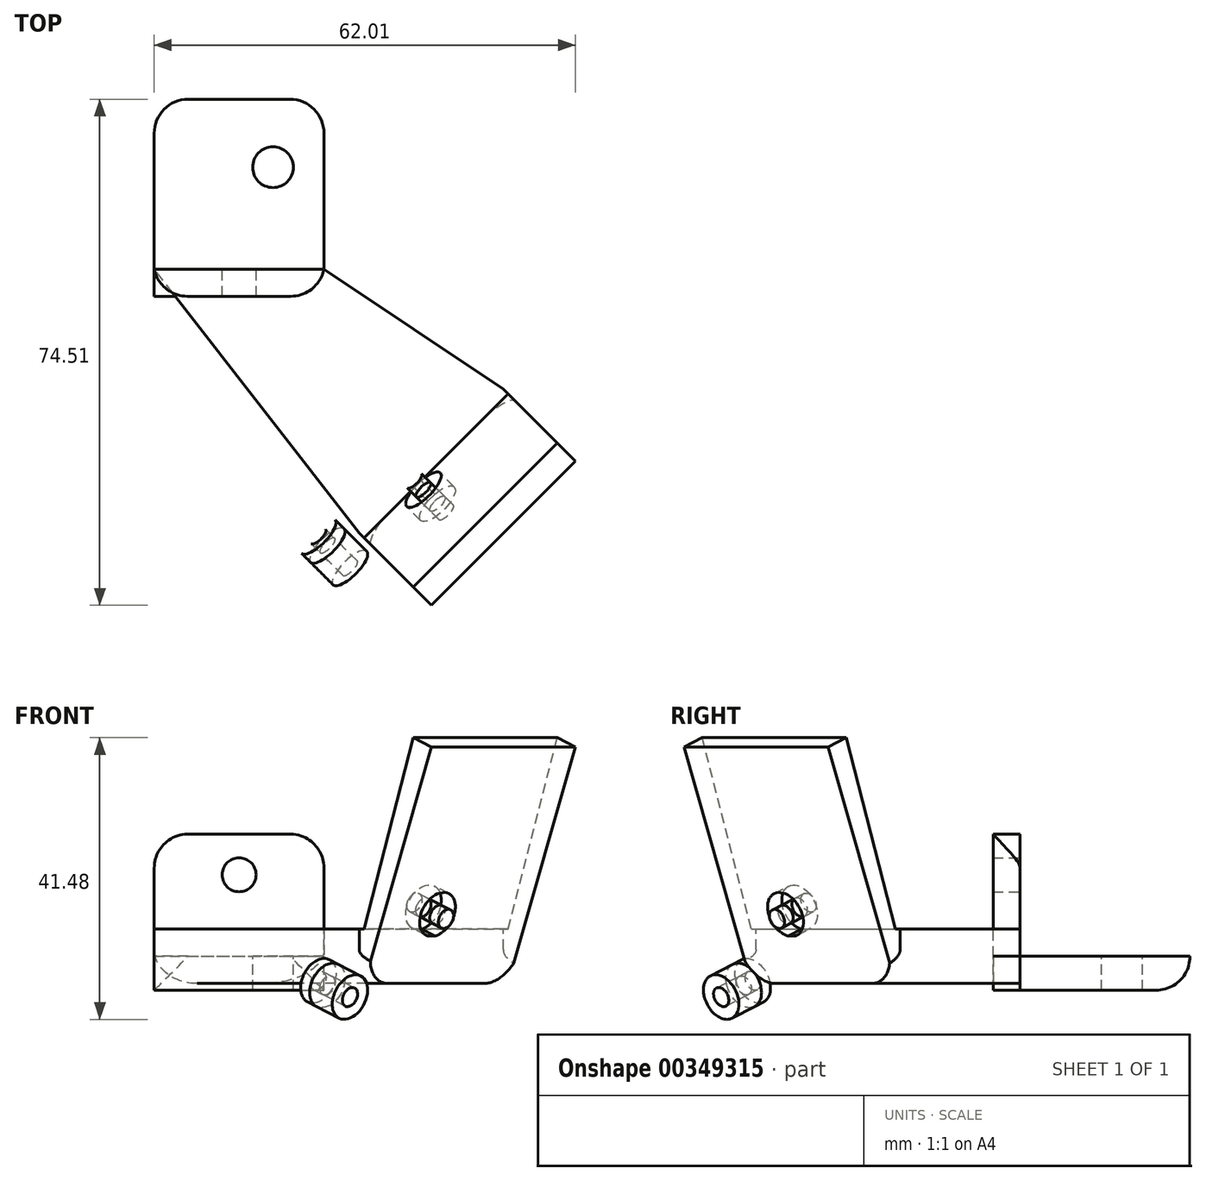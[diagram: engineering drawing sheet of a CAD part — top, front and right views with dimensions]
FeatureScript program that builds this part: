
annotation { "Feature Type Name" : "Feature", "Feature Type Description" : "" }
export const myFeature = defineFeature(function(context is Context, id is Id, definition is map)
    precondition{}
    {
        {
            var Q0;
            Q0=qCreatedBy(makeId("Top.planeOp"),FACE);
            var sketch = newSketch(context, id + "F0", { "sketchPlane" : qUnion([Q0])});
            skLineSegment(sketch, "E0.bottom", {"start": v(-12.5, 0) * mm, "end": v(12.5, 0) * mm});
            skLineSegment(sketch, "E0.top", {"start": v(-12.5, 25) * mm, "end": v(12.5, 25) * mm});
            skLineSegment(sketch, "E0.left", {"start": v(-12.5, 0) * mm, "end": v(-12.5, 25) * mm});
            skLineSegment(sketch, "E0.right", {"start": v(12.5, 0) * mm, "end": v(12.5, 25) * mm});
            skCircle(sketch, "E1", {"center": v(5, 15) * mm, "radius": 3 * mm});
            skLineSegment(sketch, "E2.top", {"start": v(-12.5, -4) * mm, "end": v(12.5, -4) * mm});
            skLineSegment(sketch, "E2.left", {"start": v(-12.5, 0) * mm, "end": v(-12.5, -4) * mm});
            skLineSegment(sketch, "E2.right", {"start": v(12.5, 0) * mm, "end": v(12.5, -4) * mm});
            skSolve(sketch);
        }
        {
            var Q0;
            Q0=makeQuery(id+"F0.imprint","IMPRINT",FACE,{"disambiguationData":[TD([[makeQuery(id+"F0.imprint","IMPRINT",EDGE,{"derivedFrom":sQuery(id+"F0.wireOp",EDGE,"E0.top")}),-1.0]])]});
            extrude(context, id + "F1", {"entities" : qUnion([Q0]), "oppositeDirection" : true, "depth" : 5 * mm});
        }
        {
            var Q0;
            Q0=makeQuery(id+"F0.imprint","IMPRINT",FACE,{"disambiguationData":[TD([[makeQuery(id+"F0.imprint","IMPRINT",EDGE,{"derivedFrom":sQuery(id+"F0.wireOp",EDGE,"E0.bottom")}),-1.0]])]});
            extrude(context, id + "F2", {"entities" : qUnion([Q0]), "depth" : 18 * mm});
        }
        {
            var Q0;
            Q0=makeQuery(id+"F2.opExtrude","CAP_FACE",FACE,{"disambiguationData":[OSD([sQuery(id+"F0.wireOp",EDGE,"E0.bottom"),sQuery(id+"F0.wireOp",EDGE,"E2.top"),sQuery(id+"F0.wireOp",EDGE,"E2.left"),sQuery(id+"F0.wireOp",EDGE,"E2.right")])],"isStart":true});
            extrude(context, id + "F3", {"entities" : qUnion([Q0]), "depth" : 5 * mm});
        }
        {
            var Q0;
            Q0=makeQuery(id+"F2.opExtrude","SWEPT_FACE",FACE,{"disambiguationData":[OSD([sQuery(id+"F0.wireOp",EDGE,"E0.bottom")])]});
            var sketch = newSketch(context, id + "F4", { "sketchPlane" : qUnion([Q0])});
            skCircle(sketch, "E3", {"center": v(0, 12) * mm, "radius": 2.5 * mm});
            skSolve(sketch);
        }
        {
            var Q0;
            Q0=makeQuery(id+"F4.imprint","IMPRINT",FACE,{"disambiguationData":[TD([[makeQuery(id+"F4.imprint","IMPRINT",EDGE,{"derivedFrom":sQuery(id+"F4.wireOp",EDGE,"E3")}),1.0]])]});
            extrude(context, id + "F5", {"entities" : qUnion([Q0]), "operationType" : NewBodyOperationType.REMOVE, "oppositeDirection" : true, "depth" : 4 * mm});
        }
        {
            var Q0;
            Q0=qCreatedBy(makeId("Top.planeOp"),FACE);
            var sketch = newSketch(context, id + "F6", { "sketchPlane" : qUnion([Q0])});
            skLineSegment(sketch, "E4", {"start": v(0, 0) * mm, "end": v(28.28, -28.28) * mm});
            skLineSegment(sketch, "E5", {"start": v(0, 0) * mm, "end": v(-12.5, 0) * mm});
            skLineSegment(sketch, "E6", {"start": v(17.68, -38.9) * mm, "end": v(28.28, -28.28) * mm});
            skLineSegment(sketch, "E7.MirrorCS", {"start": v(38.9, -17.68) * mm, "end": v(28.28, -28.28) * mm});
            skLineSegment(sketch, "E8", {"start": v(0, 0) * mm, "end": v(12.5, 0) * mm});
            skLineSegment(sketch, "E9", {"start": v(17.68, -38.9) * mm, "end": v(-12.5, 0) * mm});
            skLineSegment(sketch, "E10", {"start": v(38.9, -17.68) * mm, "end": v(12.5, 0) * mm});
            skSolve(sketch);
        }
        {
            var Q0;
            Q0=makeQuery(id+"F6.imprint","IMPRINT",FACE,{"disambiguationData":[TD([[makeQuery(id+"F6.imprint","IMPRINT",EDGE,{"derivedFrom":sQuery(id+"F6.wireOp",EDGE,"E4")}),-1.0]])]});
            var Q1;
            Q1=makeQuery(id+"F6.imprint","IMPRINT",FACE,{"disambiguationData":[TD([[makeQuery(id+"F6.imprint","IMPRINT",EDGE,{"derivedFrom":sQuery(id+"F6.wireOp",EDGE,"E4")}),1.0]])]});
            extrude(context, id + "F7", {"entities" : qUnion([Q0, Q1]), "endBound" : BoundingType.SYMMETRIC, "oppositeDirection" : true, "depth" : 8 * mm});
        }
        {
            var Q0;
            Q0=makeQuery(id+"F7.opExtrude","SWEPT_FACE",FACE,{"disambiguationData":[OSD([sQuery(id+"F6.wireOp",EDGE,"E6"),sQuery(id+"F6.wireOp",EDGE,"E7.MirrorCS")])]});
            var sketch = newSketch(context, id + "F8", { "sketchPlane" : qUnion([Q0])});
            skLineSegment(sketch, "E11.bottom", {"start": v(15, -4) * mm, "end": v(-15, -4) * mm});
            skLineSegment(sketch, "E11.top", {"start": v(15, 4) * mm, "end": v(-15, 4) * mm});
            skLineSegment(sketch, "E11.left", {"start": v(15, -4) * mm, "end": v(15, 4) * mm});
            skLineSegment(sketch, "E11.right", {"start": v(-15, -4) * mm, "end": v(-15, 4) * mm});
            skSolve(sketch);
        }
        {
            var Q0;
            Q0=makeQuery(id+"F8.imprint","IMPRINT",FACE,{"disambiguationData":[TD([[makeQuery(id+"F8.imprint","IMPRINT",EDGE,{"derivedFrom":sQuery(id+"F8.wireOp",EDGE,"E11.bottom")}),1.0]])]});
            extrude(context, id + "F9", {"entities" : qUnion([Q0]), "operationType" : NewBodyOperationType.ADD, "depth" : 1 * mm});
        }
        {
            var Q0;
            Q0=makeQuery(id+"F9.opExtrude","SWEPT_FACE",FACE,{"disambiguationData":[OSD([sQuery(id+"F8.wireOp",EDGE,"E11.left")])]});
            var sketch = newSketch(context, id + "F10", { "sketchPlane" : qUnion([Q0])});
            skLineSegment(sketch, "E12", {"start": v(-41, 4) * mm, "end": v(-51.26, 32.2) * mm});
            skLineSegment(sketch, "E13", {"start": v(-51.26, 32.2) * mm, "end": v(-55.02, 30.82) * mm});
            skLineSegment(sketch, "E14", {"start": v(-55.02, 30.82) * mm, "end": v(-41, -4) * mm});
            skSolve(sketch);
        }
        {
            var Q0;
            Q0=makeQuery(id+"F10.imprint","IMPRINT",FACE,{"disambiguationData":[TD([[makeQuery(id+"F10.imprint","IMPRINT",EDGE,{"derivedFrom":sQuery(id+"F10.wireOp",EDGE,"E12")}),1.0]])]});
            var Q1;
            Q1=makeQuery(id+"F9.opExtrude","SWEPT_FACE",FACE,{"disambiguationData":[OSD([sQuery(id+"F8.wireOp",EDGE,"E11.right")])]});
            extrude(context, id + "F11", {"entities" : qUnion([Q0]), "operationType" : NewBodyOperationType.ADD, "endBound" : BoundingType.UP_TO_SURFACE, "oppositeDirection" : true, "endBoundEntityFace" : qUnion([Q1]), "depth" : 25 * mm});
        }
        {
            var Q0;
            Q0=makeQuery(id+"F1.opExtrude","CAP_EDGE",EDGE,{"disambiguationData":[OSD([sQuery(id+"F0.wireOp",EDGE,"E0.top")])],"isStart":false});
            var Q1;
            Q1=makeQuery(id+"F2.opExtrude","SWEPT_EDGE",EDGE,{"disambiguationData":[OSD([sQuery(id+"F0.wireOp",EDGE,"E2.top"),sQuery(id+"F0.wireOp",EDGE,"E2.right")])]});
            var Q2;
            Q2=makeQuery(id+"F7.opExtrude","CAP_EDGE",EDGE,{"disambiguationData":[OSD([sQuery(id+"F6.wireOp",EDGE,"E9")])],"isStart":false});
            var Q3;
            Q3=makeQuery(id+"F7.opExtrude","CAP_EDGE",EDGE,{"disambiguationData":[OSD([sQuery(id+"F6.wireOp",EDGE,"E10")])],"isStart":false});
            var Q4;
            Q4=makeQuery(id+"F3.opExtrude","SWEPT_EDGE",EDGE,{"disambiguationData":[OSD([sQuery(id+"F0.wireOp",EDGE,"E2.top"),sQuery(id+"F0.wireOp",EDGE,"E2.right")])]});
            var Q5;
            Q5=makeQuery(id+"F2.opExtrude","CAP_EDGE",EDGE,{"disambiguationData":[OSD([sQuery(id+"F0.wireOp",EDGE,"E2.left")])],"isStart":false});
            var Q6;
            Q6=makeQuery(id+"F1.opExtrude","SWEPT_EDGE",EDGE,{"disambiguationData":[OSD([sQuery(id+"F0.wireOp",EDGE,"E0.top"),sQuery(id+"F0.wireOp",EDGE,"E0.right")])]});
            var Q7;
            Q7=makeQuery(id+"F1.opExtrude","SWEPT_EDGE",EDGE,{"disambiguationData":[OSD([sQuery(id+"F0.wireOp",EDGE,"E0.top"),sQuery(id+"F0.wireOp",EDGE,"E0.left")])]});
            var Q8;
            Q8=makeQuery(id+"F2.opExtrude","CAP_EDGE",EDGE,{"disambiguationData":[OSD([sQuery(id+"F0.wireOp",EDGE,"E2.right")])],"isStart":false});
            var Q9;
            Q9=makeQuery(id+"F2.opExtrude","SWEPT_EDGE",EDGE,{"disambiguationData":[OSD([sQuery(id+"F0.wireOp",EDGE,"E2.top"),sQuery(id+"F0.wireOp",EDGE,"E2.left")])]});
            fillet(context, id + "F12", {"entities" : qUnion([Q0, Q1, Q2, Q3, Q4, Q5, Q6, Q7, Q8, Q9]), "radius" : 5 * mm, "tangentPropagation" : true, "allowEdgeOverflow" : false});
        }
        {
            var Q0;
            Q0=makeQuery(id+"F11.opExtrude","SWEPT_FACE",FACE,{"disambiguationData":[OSD([sQuery(id+"F10.wireOp",EDGE,"E12")])]});
            var sketch = newSketch(context, id + "F13", { "sketchPlane" : qUnion([Q0])});
            skLineSegment(sketch, "E15", {"start": v(15.46, 45.21) * mm, "end": v(5.75, 16.82) * mm});
            skLineSegment(sketch, "E16", {"start": v(15.46, 45.21) * mm, "end": v(13.84, 40.48) * mm});
            skLineSegment(sketch, "E17", {"start": v(15.46, 45.21) * mm, "end": v(6.18, 18.05) * mm});
            skLineSegment(sketch, "E18", {"start": v(6.18, 18.05) * mm, "end": v(15.64, 14.82) * mm});
            skCircle(sketch, "E19", {"center": v(13.84, 40.48) * mm, "radius": 1.5 * mm});
            skCircle(sketch, "E20", {"center": v(15.64, 14.82) * mm, "radius": 1.5 * mm});
            skCircle(sketch, "E21.MirrorC", {"center": v(-3.29, 21.3) * mm, "radius": 1.5 * mm});
            skCircle(sketch, "E22", {"center": v(-3.29, 21.3) * mm, "radius": 3.5 * mm});
            skCircle(sketch, "E23", {"center": v(15.64, 14.82) * mm, "radius": 3.5 * mm});
            skCircle(sketch, "E24", {"center": v(13.84, 40.48) * mm, "radius": 3.5 * mm});
            skSolve(sketch);
        }
        {
            var Q0;
            {var subQ0=sQuery(id+"F13.wireOp",EDGE,"E20");var subQ1=sQuery(id+"F8.wireOp",EDGE,"E11.top");var subQ2=makeQuery(id+"F11.boolean.opBoolean","MERGE",EDGE,{"derivedFrom":[makeQuery(id+"F9.opExtrude","CAP_EDGE",EDGE,{"disambiguationData":[OSD([subQ1])],"isStart":false}),makeQuery(id+"F11.opExtrude","SWEPT_EDGE",EDGE,{"disambiguationData":[OSD([subQ1,sQuery(id+"F8.wireOp",EDGE,"E11.left"),sQuery(id+"F10.wireOp",EDGE,"E12")])]})]});var subQ3=makeQuery(id+"F13.imprint","INTERSECT",VERTEX,{"disambiguationData":[OD(0.0)],"derivedFrom":[subQ2,subQ0]});Q0=makeQuery(id+"F13.imprint","IMPRINT",FACE,{"disambiguationData":[TD([[makeQuery(id+"F13.imprint","IMPRINT",EDGE,{"disambiguationData":[TD([[subQ3,-1.0]])],"derivedFrom":subQ0}),-1.0]])]});}
            var Q1;
            {var subQ0=sQuery(id+"F13.wireOp",EDGE,"E20");var subQ1=sQuery(id+"F13.wireOp",EDGE,"E18");var subQ2=makeQuery(id+"F13.imprint","INTERSECT",VERTEX,{"derivedFrom":[subQ1,subQ0]});Q1=makeQuery(id+"F13.imprint","IMPRINT",FACE,{"disambiguationData":[TD([[makeQuery(id+"F13.imprint","IMPRINT",EDGE,{"disambiguationData":[TD([[subQ2,1.0]])],"derivedFrom":subQ1}),-1.0]])]});}
            var Q2;
            {var subQ0=sQuery(id+"F13.wireOp",EDGE,"E20");var subQ1=sQuery(id+"F13.wireOp",EDGE,"E18");var subQ2=makeQuery(id+"F13.imprint","INTERSECT",VERTEX,{"derivedFrom":[subQ1,subQ0]});Q2=makeQuery(id+"F13.imprint","IMPRINT",FACE,{"disambiguationData":[TD([[makeQuery(id+"F13.imprint","IMPRINT",EDGE,{"disambiguationData":[TD([[subQ2,1.0]])],"derivedFrom":subQ1}),1.0]])]});}
            var Q3;
            {var subQ0=sQuery(id+"F13.wireOp",EDGE,"E21.MirrorC");var subQ1=sQuery(id+"F8.wireOp",EDGE,"E11.top");var subQ2=makeQuery(id+"F11.boolean.opBoolean","MERGE",EDGE,{"derivedFrom":[makeQuery(id+"F9.opExtrude","CAP_EDGE",EDGE,{"disambiguationData":[OSD([subQ1])],"isStart":false}),makeQuery(id+"F11.opExtrude","SWEPT_EDGE",EDGE,{"disambiguationData":[OSD([subQ1,sQuery(id+"F8.wireOp",EDGE,"E11.left"),sQuery(id+"F10.wireOp",EDGE,"E12")])]})]});var subQ3=makeQuery(id+"F13.imprint","INTERSECT",VERTEX,{"disambiguationData":[OD(0.0)],"derivedFrom":[subQ2,subQ0]});Q3=makeQuery(id+"F13.imprint","IMPRINT",FACE,{"disambiguationData":[TD([[makeQuery(id+"F13.imprint","IMPRINT",EDGE,{"disambiguationData":[TD([[subQ3,1.0]])],"derivedFrom":subQ0}),1.0]])]});}
            var Q4;
            {var subQ0=sQuery(id+"F13.wireOp",EDGE,"E21.MirrorC");var subQ1=sQuery(id+"F8.wireOp",EDGE,"E11.top");var subQ2=makeQuery(id+"F11.boolean.opBoolean","MERGE",EDGE,{"derivedFrom":[makeQuery(id+"F9.opExtrude","CAP_EDGE",EDGE,{"disambiguationData":[OSD([subQ1])],"isStart":false}),makeQuery(id+"F11.opExtrude","SWEPT_EDGE",EDGE,{"disambiguationData":[OSD([subQ1,sQuery(id+"F8.wireOp",EDGE,"E11.left"),sQuery(id+"F10.wireOp",EDGE,"E12")])]})]});var subQ3=makeQuery(id+"F13.imprint","INTERSECT",VERTEX,{"disambiguationData":[OD(0.0)],"derivedFrom":[subQ2,subQ0]});Q4=makeQuery(id+"F13.imprint","IMPRINT",FACE,{"disambiguationData":[TD([[makeQuery(id+"F13.imprint","IMPRINT",EDGE,{"disambiguationData":[TD([[subQ3,-1.0]])],"derivedFrom":subQ0}),1.0]])]});}
            var Q5;
            {var subQ0=sQuery(id+"F13.wireOp",EDGE,"E24");var subQ1=sQuery(id+"F13.wireOp",EDGE,"E17");var subQ2=makeQuery(id+"F13.imprint","INTERSECT",VERTEX,{"disambiguationData":[OD(0.0)],"derivedFrom":[subQ1,subQ0]});Q5=makeQuery(id+"F13.imprint","IMPRINT",FACE,{"disambiguationData":[TD([[makeQuery(id+"F13.imprint","IMPRINT",EDGE,{"disambiguationData":[TD([[subQ2,-1.0]])],"derivedFrom":subQ1}),1.0]])]});}
            var Q6;
            {var subQ0=sQuery(id+"F13.wireOp",EDGE,"E24");var subQ1=sQuery(id+"F13.wireOp",EDGE,"E17");var subQ2=makeQuery(id+"F13.imprint","INTERSECT",VERTEX,{"disambiguationData":[OD(0.0)],"derivedFrom":[subQ1,subQ0]});Q6=makeQuery(id+"F13.imprint","IMPRINT",FACE,{"disambiguationData":[TD([[makeQuery(id+"F13.imprint","IMPRINT",EDGE,{"disambiguationData":[TD([[subQ2,-1.0]])],"derivedFrom":subQ1}),-1.0]])]});}
            extrude(context, id + "F14", {"entities" : qUnion([Q0, Q1, Q2, Q3, Q4, Q5, Q6]), "depth" : 2 * mm});
        }
        {
            var Q0;
            {var subQ0=sQuery(id+"F13.wireOp",EDGE,"E20");var subQ1=makeQuery(id+"F13.imprint","INTERSECT",VERTEX,{"derivedFrom":[sQuery(id+"F13.wireOp",EDGE,"E18"),subQ0]});Q0=makeQuery(id+"F13.imprint","IMPRINT",FACE,{"disambiguationData":[TD([[makeQuery(id+"F13.imprint","IMPRINT",EDGE,{"disambiguationData":[TD([[subQ1,-1.0]])],"derivedFrom":subQ0}),1.0]])]});}
            var Q1;
            {var subQ0=sQuery(id+"F13.wireOp",EDGE,"E20");var subQ1=sQuery(id+"F8.wireOp",EDGE,"E11.top");var subQ2=makeQuery(id+"F11.boolean.opBoolean","MERGE",EDGE,{"derivedFrom":[makeQuery(id+"F9.opExtrude","CAP_EDGE",EDGE,{"disambiguationData":[OSD([subQ1])],"isStart":false}),makeQuery(id+"F11.opExtrude","SWEPT_EDGE",EDGE,{"disambiguationData":[OSD([subQ1,sQuery(id+"F8.wireOp",EDGE,"E11.left"),sQuery(id+"F10.wireOp",EDGE,"E12")])]})]});var subQ3=makeQuery(id+"F13.imprint","INTERSECT",VERTEX,{"disambiguationData":[OD(0.0)],"derivedFrom":[subQ2,subQ0]});Q1=makeQuery(id+"F13.imprint","IMPRINT",FACE,{"disambiguationData":[TD([[makeQuery(id+"F13.imprint","IMPRINT",EDGE,{"disambiguationData":[TD([[subQ3,-1.0]])],"derivedFrom":subQ0}),1.0]])]});}
            var Q2;
            {var subQ0=sQuery(id+"F13.wireOp",EDGE,"E21.MirrorC");var subQ1=sQuery(id+"F8.wireOp",EDGE,"E11.top");var subQ2=makeQuery(id+"F11.boolean.opBoolean","MERGE",EDGE,{"derivedFrom":[makeQuery(id+"F9.opExtrude","CAP_EDGE",EDGE,{"disambiguationData":[OSD([subQ1])],"isStart":false}),makeQuery(id+"F11.opExtrude","SWEPT_EDGE",EDGE,{"disambiguationData":[OSD([subQ1,sQuery(id+"F8.wireOp",EDGE,"E11.left"),sQuery(id+"F10.wireOp",EDGE,"E12")])]})]});var subQ3=makeQuery(id+"F13.imprint","INTERSECT",VERTEX,{"disambiguationData":[OD(0.0)],"derivedFrom":[subQ2,subQ0]});Q2=makeQuery(id+"F13.imprint","IMPRINT",FACE,{"disambiguationData":[TD([[makeQuery(id+"F13.imprint","IMPRINT",EDGE,{"disambiguationData":[TD([[subQ3,1.0]])],"derivedFrom":subQ0}),-1.0]])]});}
            var Q3;
            {var subQ0=sQuery(id+"F13.wireOp",EDGE,"E21.MirrorC");var subQ1=sQuery(id+"F8.wireOp",EDGE,"E11.top");var subQ2=makeQuery(id+"F11.boolean.opBoolean","MERGE",EDGE,{"derivedFrom":[makeQuery(id+"F9.opExtrude","CAP_EDGE",EDGE,{"disambiguationData":[OSD([subQ1])],"isStart":false}),makeQuery(id+"F11.opExtrude","SWEPT_EDGE",EDGE,{"disambiguationData":[OSD([subQ1,sQuery(id+"F8.wireOp",EDGE,"E11.left"),sQuery(id+"F10.wireOp",EDGE,"E12")])]})]});var subQ3=makeQuery(id+"F13.imprint","INTERSECT",VERTEX,{"disambiguationData":[OD(0.0)],"derivedFrom":[subQ2,subQ0]});Q3=makeQuery(id+"F13.imprint","IMPRINT",FACE,{"disambiguationData":[TD([[makeQuery(id+"F13.imprint","IMPRINT",EDGE,{"disambiguationData":[TD([[subQ3,-1.0]])],"derivedFrom":subQ0}),-1.0]])]});}
            var Q4;
            {var subQ0=sQuery(id+"F13.wireOp",EDGE,"E17");var subQ1=makeQuery(id+"F13.imprint","IMPRINT",VERTEX,{"derivedFrom":subQ0});Q4=makeQuery(id+"F13.imprint","IMPRINT",FACE,{"disambiguationData":[TD([[makeQuery(id+"F13.imprint","IMPRINT",EDGE,{"disambiguationData":[TD([[subQ1,1.0]])],"derivedFrom":subQ0}),1.0]])]});}
            var Q5;
            {var subQ0=sQuery(id+"F13.wireOp",EDGE,"E17");var subQ1=makeQuery(id+"F13.imprint","IMPRINT",VERTEX,{"derivedFrom":subQ0});Q5=makeQuery(id+"F13.imprint","IMPRINT",FACE,{"disambiguationData":[TD([[makeQuery(id+"F13.imprint","IMPRINT",EDGE,{"disambiguationData":[TD([[subQ1,1.0]])],"derivedFrom":subQ0}),-1.0]])]});}
            extrude(context, id + "F15", {"entities" : qUnion([Q0, Q1, Q2, Q3, Q4, Q5]), "operationType" : NewBodyOperationType.REMOVE, "endBound" : BoundingType.SYMMETRIC, "oppositeDirection" : true, "depth" : 40 * mm});
        }
        {
            var Q0;
            Q0=makeQuery(id+"F14.opExtrude","CAP_FACE",FACE,{"disambiguationData":[OSD([sQuery(id+"F13.wireOp",EDGE,"E20"),sQuery(id+"F13.wireOp",EDGE,"E23")])],"isStart":false});
            var Q1;
            Q1=makeQuery(id+"F14.opExtrude","CAP_FACE",FACE,{"disambiguationData":[OSD([sQuery(id+"F13.wireOp",EDGE,"E21.MirrorC"),sQuery(id+"F13.wireOp",EDGE,"E22")])],"isStart":false});
            extrude(context, id + "F16", {"entities" : qUnion([Q0, Q1]), "operationType" : NewBodyOperationType.REMOVE, "depth" : 10 * mm});
        }
        {
            var Q0;
            {var subQ0=sQuery(id+"F13.wireOp",EDGE,"E20");var subQ1=sQuery(id+"F8.wireOp",EDGE,"E11.top");var subQ2=makeQuery(id+"F11.boolean.opBoolean","MERGE",EDGE,{"derivedFrom":[makeQuery(id+"F9.opExtrude","CAP_EDGE",EDGE,{"disambiguationData":[OSD([subQ1])],"isStart":false}),makeQuery(id+"F11.opExtrude","SWEPT_EDGE",EDGE,{"disambiguationData":[OSD([subQ1,sQuery(id+"F8.wireOp",EDGE,"E11.left"),sQuery(id+"F10.wireOp",EDGE,"E12")])]})]});var subQ3=makeQuery(id+"F13.imprint","INTERSECT",VERTEX,{"disambiguationData":[OD(0.0)],"derivedFrom":[subQ2,subQ0]});Q0=makeQuery(id+"F13.imprint","IMPRINT",FACE,{"disambiguationData":[TD([[makeQuery(id+"F13.imprint","IMPRINT",EDGE,{"disambiguationData":[TD([[subQ3,-1.0]])],"derivedFrom":subQ0}),-1.0]])]});}
            var Q1;
            {var subQ0=sQuery(id+"F13.wireOp",EDGE,"E20");var subQ1=sQuery(id+"F13.wireOp",EDGE,"E18");var subQ2=makeQuery(id+"F13.imprint","INTERSECT",VERTEX,{"derivedFrom":[subQ1,subQ0]});Q1=makeQuery(id+"F13.imprint","IMPRINT",FACE,{"disambiguationData":[TD([[makeQuery(id+"F13.imprint","IMPRINT",EDGE,{"disambiguationData":[TD([[subQ2,1.0]])],"derivedFrom":subQ1}),-1.0]])]});}
            var Q2;
            {var subQ0=sQuery(id+"F13.wireOp",EDGE,"E20");var subQ1=sQuery(id+"F13.wireOp",EDGE,"E18");var subQ2=makeQuery(id+"F13.imprint","INTERSECT",VERTEX,{"derivedFrom":[subQ1,subQ0]});Q2=makeQuery(id+"F13.imprint","IMPRINT",FACE,{"disambiguationData":[TD([[makeQuery(id+"F13.imprint","IMPRINT",EDGE,{"disambiguationData":[TD([[subQ2,1.0]])],"derivedFrom":subQ1}),1.0]])]});}
            var Q3;
            {var subQ0=sQuery(id+"F13.wireOp",EDGE,"E21.MirrorC");var subQ1=sQuery(id+"F8.wireOp",EDGE,"E11.top");var subQ2=makeQuery(id+"F11.boolean.opBoolean","MERGE",EDGE,{"derivedFrom":[makeQuery(id+"F9.opExtrude","CAP_EDGE",EDGE,{"disambiguationData":[OSD([subQ1])],"isStart":false}),makeQuery(id+"F11.opExtrude","SWEPT_EDGE",EDGE,{"disambiguationData":[OSD([subQ1,sQuery(id+"F8.wireOp",EDGE,"E11.left"),sQuery(id+"F10.wireOp",EDGE,"E12")])]})]});var subQ3=makeQuery(id+"F13.imprint","INTERSECT",VERTEX,{"disambiguationData":[OD(0.0)],"derivedFrom":[subQ2,subQ0]});Q3=makeQuery(id+"F13.imprint","IMPRINT",FACE,{"disambiguationData":[TD([[makeQuery(id+"F13.imprint","IMPRINT",EDGE,{"disambiguationData":[TD([[subQ3,-1.0]])],"derivedFrom":subQ0}),1.0]])]});}
            var Q4;
            {var subQ0=sQuery(id+"F13.wireOp",EDGE,"E21.MirrorC");var subQ1=sQuery(id+"F8.wireOp",EDGE,"E11.top");var subQ2=makeQuery(id+"F11.boolean.opBoolean","MERGE",EDGE,{"derivedFrom":[makeQuery(id+"F9.opExtrude","CAP_EDGE",EDGE,{"disambiguationData":[OSD([subQ1])],"isStart":false}),makeQuery(id+"F11.opExtrude","SWEPT_EDGE",EDGE,{"disambiguationData":[OSD([subQ1,sQuery(id+"F8.wireOp",EDGE,"E11.left"),sQuery(id+"F10.wireOp",EDGE,"E12")])]})]});var subQ3=makeQuery(id+"F13.imprint","INTERSECT",VERTEX,{"disambiguationData":[OD(0.0)],"derivedFrom":[subQ2,subQ0]});Q4=makeQuery(id+"F13.imprint","IMPRINT",FACE,{"disambiguationData":[TD([[makeQuery(id+"F13.imprint","IMPRINT",EDGE,{"disambiguationData":[TD([[subQ3,1.0]])],"derivedFrom":subQ0}),1.0]])]});}
            var Q5;
            {var subQ0=sQuery(id+"F13.wireOp",EDGE,"E24");var subQ1=sQuery(id+"F13.wireOp",EDGE,"E17");var subQ2=makeQuery(id+"F13.imprint","INTERSECT",VERTEX,{"disambiguationData":[OD(0.0)],"derivedFrom":[subQ1,subQ0]});Q5=makeQuery(id+"F13.imprint","IMPRINT",FACE,{"disambiguationData":[TD([[makeQuery(id+"F13.imprint","IMPRINT",EDGE,{"disambiguationData":[TD([[subQ2,-1.0]])],"derivedFrom":subQ1}),-1.0]])]});}
            var Q6;
            {var subQ0=sQuery(id+"F13.wireOp",EDGE,"E24");var subQ1=sQuery(id+"F13.wireOp",EDGE,"E17");var subQ2=makeQuery(id+"F13.imprint","INTERSECT",VERTEX,{"disambiguationData":[OD(0.0)],"derivedFrom":[subQ1,subQ0]});Q6=makeQuery(id+"F13.imprint","IMPRINT",FACE,{"disambiguationData":[TD([[makeQuery(id+"F13.imprint","IMPRINT",EDGE,{"disambiguationData":[TD([[subQ2,-1.0]])],"derivedFrom":subQ1}),1.0]])]});}
            extrude(context, id + "F17", {"entities" : qUnion([Q0, Q1, Q2, Q3, Q4, Q5, Q6]), "oppositeDirection" : true, "depth" : 5 * mm});
        }
    });
